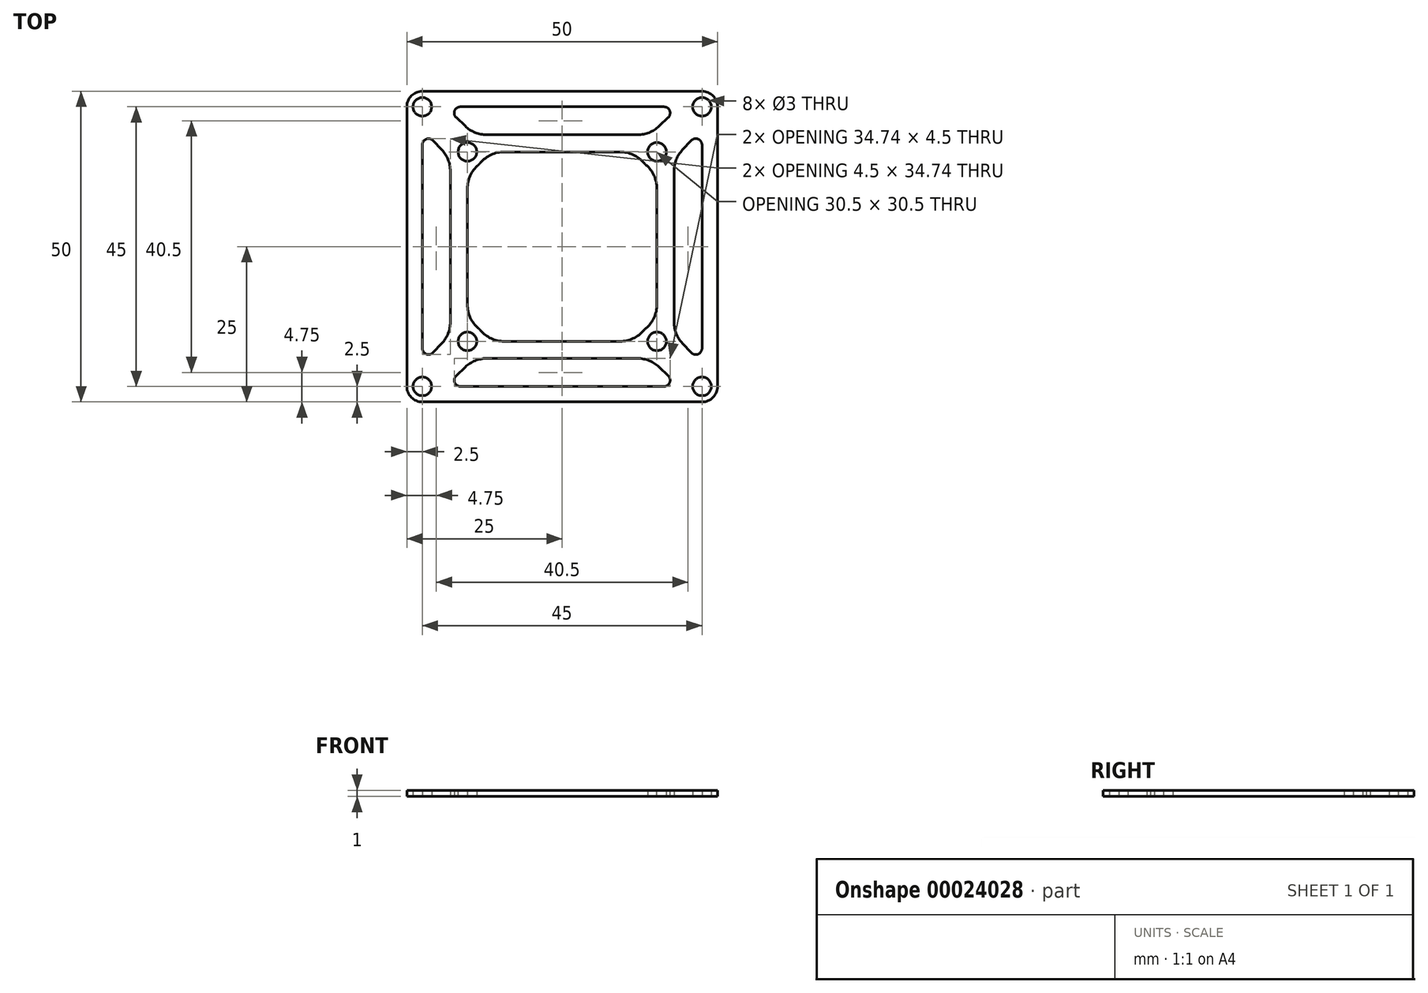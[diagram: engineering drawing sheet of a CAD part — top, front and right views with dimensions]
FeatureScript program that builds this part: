
annotation { "Feature Type Name" : "Feature", "Feature Type Description" : "" }
export const myFeature = defineFeature(function(context is Context, id is Id, definition is map)
    precondition{}
    {
        {
            var Q0;
            Q0=qCreatedBy(makeId("Top.planeOp"),FACE);
            var sketch = newSketch(context, id + "F0", { "sketchPlane" : qUnion([Q0])});
            skLineSegment(sketch, "E0.bottom", {"start": v(15.25, 15.25) * mm, "end": v(-15.25, 15.25) * mm});
            skLineSegment(sketch, "E0.top", {"start": v(15.25, -15.25) * mm, "end": v(-15.25, -15.25) * mm});
            skLineSegment(sketch, "E0.left", {"start": v(15.25, 15.25) * mm, "end": v(15.25, -15.25) * mm});
            skLineSegment(sketch, "E0.right", {"start": v(-15.25, 15.25) * mm, "end": v(-15.25, -15.25) * mm});
            skPoint(sketch, "E0.middle", {"position": v(0, 0) * mm});
            skLineSegment(sketch, "E1.bottom", {"start": v(22.5, 22.5) * mm, "end": v(-22.5, 22.5) * mm});
            skLineSegment(sketch, "E1.top", {"start": v(22.5, -22.5) * mm, "end": v(-22.5, -22.5) * mm});
            skLineSegment(sketch, "E1.left", {"start": v(22.5, 22.5) * mm, "end": v(22.5, -22.5) * mm});
            skLineSegment(sketch, "E1.right", {"start": v(-22.5, 22.5) * mm, "end": v(-22.5, -22.5) * mm});
            skLineSegment(sketch, "E2.bottom", {"start": v(-18, 18) * mm, "end": v(18, 18) * mm});
            skLineSegment(sketch, "E2.top", {"start": v(-18, -18) * mm, "end": v(18, -18) * mm});
            skLineSegment(sketch, "E2.left", {"start": v(-18, 18) * mm, "end": v(-18, -18) * mm});
            skLineSegment(sketch, "E2.right", {"start": v(18, 18) * mm, "end": v(18, -18) * mm});
            skLineSegment(sketch, "E3.bottom", {"start": v(-25, 25) * mm, "end": v(25, 25) * mm});
            skLineSegment(sketch, "E3.top", {"start": v(-25, -25) * mm, "end": v(25, -25) * mm});
            skLineSegment(sketch, "E3.left", {"start": v(-25, 25) * mm, "end": v(-25, -25) * mm});
            skLineSegment(sketch, "E3.right", {"start": v(25, 25) * mm, "end": v(25, -25) * mm});
            skCircle(sketch, "E4", {"center": v(-15.25, 15.25) * mm, "radius": 1.5 * mm});
            skCircle(sketch, "E5", {"center": v(-22.5, 22.5) * mm, "radius": 1.5 * mm});
            skLineSegment(sketch, "E6", {"start": v(0, 25) * mm, "end": v(0, 0) * mm, "construction": true});
            skLineSegment(sketch, "E7", {"start": v(0, 0) * mm, "end": v(-25, 0) * mm, "construction": true});
            skCircle(sketch, "E8.MirrorC", {"center": v(15.25, 15.25) * mm, "radius": 1.5 * mm});
            skCircle(sketch, "E9.MirrorC", {"center": v(22.5, 22.5) * mm, "radius": 1.5 * mm});
            skCircle(sketch, "E10.MirrorC", {"center": v(-15.25, -15.25) * mm, "radius": 1.5 * mm});
            skCircle(sketch, "E11.MirrorC", {"center": v(15.25, -15.25) * mm, "radius": 1.5 * mm});
            skCircle(sketch, "E12.MirrorC", {"center": v(22.5, -22.5) * mm, "radius": 1.5 * mm});
            skCircle(sketch, "E13.MirrorC", {"center": v(-22.5, -22.5) * mm, "radius": 1.5 * mm});
            skCircle(sketch, "E14", {"center": v(-22.5, 22.5) * mm, "radius": 2.5 * mm});
            skCircle(sketch, "E15", {"center": v(-15.25, 15.25) * mm, "radius": 2.75 * mm});
            skCircle(sketch, "E16.MirrorC", {"center": v(15.25, 15.25) * mm, "radius": 2.75 * mm});
            skCircle(sketch, "E17.MirrorC", {"center": v(22.5, 22.5) * mm, "radius": 2.5 * mm});
            skCircle(sketch, "E18.MirrorC", {"center": v(-15.25, -15.25) * mm, "radius": 2.75 * mm});
            skCircle(sketch, "E19.MirrorC", {"center": v(-22.5, -22.5) * mm, "radius": 2.5 * mm});
            skCircle(sketch, "E20.MirrorC", {"center": v(15.25, -15.25) * mm, "radius": 2.75 * mm});
            skCircle(sketch, "E21.MirrorC", {"center": v(22.5, -22.5) * mm, "radius": 2.5 * mm});
            skLineSegment(sketch, "E22", {"start": v(-13.35, 17.24) * mm, "end": v(-20.78, 24.31) * mm});
            skLineSegment(sketch, "E23", {"start": v(-17.24, 13.35) * mm, "end": v(-24.31, 20.78) * mm});
            skLineSegment(sketch, "E24.MirrorCS", {"start": v(13.35, 17.24) * mm, "end": v(20.78, 24.31) * mm});
            skLineSegment(sketch, "E25.MirrorCS", {"start": v(17.24, 13.35) * mm, "end": v(24.31, 20.78) * mm});
            skLineSegment(sketch, "E26.MirrorCS", {"start": v(-17.24, -13.35) * mm, "end": v(-24.31, -20.78) * mm});
            skLineSegment(sketch, "E27.MirrorCS", {"start": v(-13.35, -17.24) * mm, "end": v(-20.78, -24.31) * mm});
            skLineSegment(sketch, "E28.MirrorCS", {"start": v(17.24, -13.35) * mm, "end": v(24.31, -20.78) * mm});
            skLineSegment(sketch, "E29.MirrorCS", {"start": v(13.35, -17.24) * mm, "end": v(20.78, -24.31) * mm});
            skSolve(sketch);
        }
        {
            var Q0;
            {var subQ0=sQuery(id+"F0.wireOp",EDGE,"E17.MirrorC");var subQ1=sQuery(id+"F0.wireOp",EDGE,"E1.bottom");var subQ2=makeQuery(id+"F0.imprint","INTERSECT",VERTEX,{"derivedFrom":[subQ1,subQ0]});Q0=makeQuery(id+"F0.imprint","IMPRINT",FACE,{"disambiguationData":[TD([[makeQuery(id+"F0.imprint","IMPRINT",EDGE,{"disambiguationData":[TD([[subQ2,-1.0]])],"derivedFrom":subQ1}),-1.0]])]});}
            var Q1;
            {var subQ0=sQuery(id+"F0.wireOp",EDGE,"E21.MirrorC");var subQ1=sQuery(id+"F0.wireOp",EDGE,"E1.top");var subQ2=makeQuery(id+"F0.imprint","INTERSECT",VERTEX,{"derivedFrom":[subQ1,subQ0]});Q1=makeQuery(id+"F0.imprint","IMPRINT",FACE,{"disambiguationData":[TD([[makeQuery(id+"F0.imprint","IMPRINT",EDGE,{"disambiguationData":[TD([[subQ2,-1.0]])],"derivedFrom":subQ1}),1.0]])]});}
            var Q2;
            {var subQ0=sQuery(id+"F0.wireOp",EDGE,"E17.MirrorC");var subQ1=sQuery(id+"F0.wireOp",EDGE,"E1.left");var subQ2=makeQuery(id+"F0.imprint","INTERSECT",VERTEX,{"derivedFrom":[subQ1,subQ0]});Q2=makeQuery(id+"F0.imprint","IMPRINT",FACE,{"disambiguationData":[TD([[makeQuery(id+"F0.imprint","IMPRINT",EDGE,{"disambiguationData":[TD([[subQ2,-1.0]])],"derivedFrom":subQ1}),1.0]])]});}
            var Q3;
            {var subQ0=sQuery(id+"F0.wireOp",EDGE,"E14");var subQ1=sQuery(id+"F0.wireOp",EDGE,"E1.right");var subQ2=makeQuery(id+"F0.imprint","INTERSECT",VERTEX,{"derivedFrom":[subQ1,subQ0]});Q3=makeQuery(id+"F0.imprint","IMPRINT",FACE,{"disambiguationData":[TD([[makeQuery(id+"F0.imprint","IMPRINT",EDGE,{"disambiguationData":[TD([[subQ2,-1.0]])],"derivedFrom":subQ1}),-1.0]])]});}
            var Q4;
            {var subQ0=sQuery(id+"F0.wireOp",EDGE,"E9.MirrorC");var subQ1=sQuery(id+"F0.wireOp",EDGE,"E1.bottom");var subQ2=makeQuery(id+"F0.imprint","INTERSECT",VERTEX,{"derivedFrom":[subQ1,subQ0]});Q4=makeQuery(id+"F0.imprint","IMPRINT",FACE,{"disambiguationData":[TD([[makeQuery(id+"F0.imprint","IMPRINT",EDGE,{"disambiguationData":[TD([[subQ2,-1.0]])],"derivedFrom":subQ1}),-1.0]])]});}
            var Q5;
            {var subQ0=sQuery(id+"F0.wireOp",EDGE,"E14");var subQ2=sQuery(id+"F0.wireOp",EDGE,"E1.bottom");var subQ3=makeQuery(id+"F0.imprint","INTERSECT",VERTEX,{"derivedFrom":[subQ2,subQ0]});Q5=makeQuery(id+"F0.imprint","IMPRINT",FACE,{"disambiguationData":[TD([[makeQuery(id+"F0.imprint","IMPRINT",EDGE,{"disambiguationData":[TD([[subQ3,-1.0]])],"derivedFrom":subQ2}),-1.0]])]});}
            var Q6;
            {var subQ2=sQuery(id+"F0.wireOp",EDGE,"E1.top");var subQ4=sQuery(id+"F0.wireOp",EDGE,"E12.MirrorC");var subQ5=makeQuery(id+"F0.imprint","INTERSECT",VERTEX,{"derivedFrom":[subQ2,subQ4]});Q6=makeQuery(id+"F0.imprint","IMPRINT",FACE,{"disambiguationData":[TD([[makeQuery(id+"F0.imprint","IMPRINT",EDGE,{"disambiguationData":[TD([[subQ5,-1.0]])],"derivedFrom":subQ2}),1.0]])]});}
            var Q7;
            {var subQ1=sQuery(id+"F0.wireOp",EDGE,"E1.top");var subQ5=sQuery(id+"F0.wireOp",EDGE,"E19.MirrorC");var subQ7=makeQuery(id+"F0.imprint","INTERSECT",VERTEX,{"derivedFrom":[subQ1,subQ5]});Q7=makeQuery(id+"F0.imprint","IMPRINT",FACE,{"disambiguationData":[TD([[makeQuery(id+"F0.imprint","IMPRINT",EDGE,{"disambiguationData":[TD([[subQ7,-1.0]])],"derivedFrom":subQ1}),1.0]])]});}
            var Q8;
            {var subQ0=sQuery(id+"F0.wireOp",EDGE,"E14");var subQ1=sQuery(id+"F0.wireOp",EDGE,"E1.bottom");var subQ2=makeQuery(id+"F0.imprint","INTERSECT",VERTEX,{"derivedFrom":[subQ1,subQ0]});Q8=makeQuery(id+"F0.imprint","IMPRINT",FACE,{"disambiguationData":[TD([[makeQuery(id+"F0.imprint","IMPRINT",EDGE,{"disambiguationData":[TD([[subQ2,-1.0]])],"derivedFrom":subQ1}),1.0]])]});}
            var Q9;
            {var subQ0=sQuery(id+"F0.wireOp",EDGE,"E9.MirrorC");var subQ1=sQuery(id+"F0.wireOp",EDGE,"E1.bottom");var subQ2=makeQuery(id+"F0.imprint","INTERSECT",VERTEX,{"derivedFrom":[subQ1,subQ0]});Q9=makeQuery(id+"F0.imprint","IMPRINT",FACE,{"disambiguationData":[TD([[makeQuery(id+"F0.imprint","IMPRINT",EDGE,{"disambiguationData":[TD([[subQ2,-1.0]])],"derivedFrom":subQ1}),1.0]])]});}
            var Q10;
            {var subQ0=sQuery(id+"F0.wireOp",EDGE,"E12.MirrorC");var subQ1=sQuery(id+"F0.wireOp",EDGE,"E1.top");var subQ2=makeQuery(id+"F0.imprint","INTERSECT",VERTEX,{"derivedFrom":[subQ1,subQ0]});Q10=makeQuery(id+"F0.imprint","IMPRINT",FACE,{"disambiguationData":[TD([[makeQuery(id+"F0.imprint","IMPRINT",EDGE,{"disambiguationData":[TD([[subQ2,-1.0]])],"derivedFrom":subQ1}),-1.0]])]});}
            var Q11;
            {var subQ0=sQuery(id+"F0.wireOp",EDGE,"E19.MirrorC");var subQ1=sQuery(id+"F0.wireOp",EDGE,"E1.top");var subQ2=makeQuery(id+"F0.imprint","INTERSECT",VERTEX,{"derivedFrom":[subQ1,subQ0]});Q11=makeQuery(id+"F0.imprint","IMPRINT",FACE,{"disambiguationData":[TD([[makeQuery(id+"F0.imprint","IMPRINT",EDGE,{"disambiguationData":[TD([[subQ2,-1.0]])],"derivedFrom":subQ1}),-1.0]])]});}
            var Q12;
            {var subQ16=sQuery(id+"F0.wireOp",EDGE,"E1.bottom");var subQ30=sQuery(id+"F0.wireOp",EDGE,"E17.MirrorC");var subQ31=makeQuery(id+"F0.imprint","INTERSECT",VERTEX,{"derivedFrom":[subQ16,subQ30]});Q12=makeQuery(id+"F0.imprint","IMPRINT",FACE,{"disambiguationData":[TD([[makeQuery(id+"F0.imprint","IMPRINT",EDGE,{"disambiguationData":[TD([[subQ31,-1.0]])],"derivedFrom":subQ16}),1.0]])]});}
            var Q13;
            {var subQ0=sQuery(id+"F0.wireOp",EDGE,"E18.MirrorC");var subQ1=sQuery(id+"F0.wireOp",EDGE,"E0.top");var subQ2=makeQuery(id+"F0.imprint","INTERSECT",VERTEX,{"derivedFrom":[subQ1,subQ0]});Q13=makeQuery(id+"F0.imprint","IMPRINT",FACE,{"disambiguationData":[TD([[makeQuery(id+"F0.imprint","IMPRINT",EDGE,{"disambiguationData":[TD([[subQ2,-1.0]])],"derivedFrom":subQ1}),-1.0]])]});}
            var Q14;
            {var subQ0=sQuery(id+"F0.wireOp",EDGE,"E18.MirrorC");var subQ1=sQuery(id+"F0.wireOp",EDGE,"E0.top");var subQ2=makeQuery(id+"F0.imprint","INTERSECT",VERTEX,{"derivedFrom":[subQ1,subQ0]});Q14=makeQuery(id+"F0.imprint","IMPRINT",FACE,{"disambiguationData":[TD([[makeQuery(id+"F0.imprint","IMPRINT",EDGE,{"disambiguationData":[TD([[subQ2,-1.0]])],"derivedFrom":subQ1}),1.0]])]});}
            var Q15;
            {var subQ0=sQuery(id+"F0.wireOp",EDGE,"E2.left");var subQ1=sQuery(id+"F0.wireOp",EDGE,"E2.top");var subQ2=makeQuery(id+"F0.imprint","INTERSECT",VERTEX,{"derivedFrom":[subQ1,subQ0]});Q15=makeQuery(id+"F0.imprint","IMPRINT",FACE,{"disambiguationData":[TD([[makeQuery(id+"F0.imprint","IMPRINT",EDGE,{"disambiguationData":[TD([[subQ2,-1.0]])],"derivedFrom":subQ1}),1.0]])]});}
            var Q16;
            {var subQ0=sQuery(id+"F0.wireOp",EDGE,"E20.MirrorC");var subQ1=sQuery(id+"F0.wireOp",EDGE,"E0.top");var subQ2=makeQuery(id+"F0.imprint","INTERSECT",VERTEX,{"derivedFrom":[subQ1,subQ0]});Q16=makeQuery(id+"F0.imprint","IMPRINT",FACE,{"disambiguationData":[TD([[makeQuery(id+"F0.imprint","IMPRINT",EDGE,{"disambiguationData":[TD([[subQ2,-1.0]])],"derivedFrom":subQ1}),1.0]])]});}
            var Q17;
            {var subQ0=sQuery(id+"F0.wireOp",EDGE,"E15");var subQ1=sQuery(id+"F0.wireOp",EDGE,"E0.right");var subQ2=makeQuery(id+"F0.imprint","INTERSECT",VERTEX,{"derivedFrom":[subQ1,subQ0]});Q17=makeQuery(id+"F0.imprint","IMPRINT",FACE,{"disambiguationData":[TD([[makeQuery(id+"F0.imprint","IMPRINT",EDGE,{"disambiguationData":[TD([[subQ2,-1.0]])],"derivedFrom":subQ1}),-1.0]])]});}
            var Q18;
            {var subQ0=sQuery(id+"F0.wireOp",EDGE,"E16.MirrorC");var subQ1=sQuery(id+"F0.wireOp",EDGE,"E0.bottom");var subQ2=makeQuery(id+"F0.imprint","INTERSECT",VERTEX,{"derivedFrom":[subQ1,subQ0]});Q18=makeQuery(id+"F0.imprint","IMPRINT",FACE,{"disambiguationData":[TD([[makeQuery(id+"F0.imprint","IMPRINT",EDGE,{"disambiguationData":[TD([[subQ2,-1.0]])],"derivedFrom":subQ1}),-1.0]])]});}
            var Q19;
            {var subQ0=sQuery(id+"F0.wireOp",EDGE,"E16.MirrorC");var subQ1=sQuery(id+"F0.wireOp",EDGE,"E0.left");var subQ2=makeQuery(id+"F0.imprint","INTERSECT",VERTEX,{"derivedFrom":[subQ1,subQ0]});Q19=makeQuery(id+"F0.imprint","IMPRINT",FACE,{"disambiguationData":[TD([[makeQuery(id+"F0.imprint","IMPRINT",EDGE,{"disambiguationData":[TD([[subQ2,-1.0]])],"derivedFrom":subQ1}),1.0]])]});}
            var Q20;
            {var subQ1=sQuery(id+"F0.wireOp",EDGE,"E0.top");var subQ4=sQuery(id+"F0.wireOp",EDGE,"E11.MirrorC");var subQ5=makeQuery(id+"F0.imprint","INTERSECT",VERTEX,{"derivedFrom":[subQ1,subQ4]});Q20=makeQuery(id+"F0.imprint","IMPRINT",FACE,{"disambiguationData":[TD([[makeQuery(id+"F0.imprint","IMPRINT",EDGE,{"disambiguationData":[TD([[subQ5,-1.0]])],"derivedFrom":subQ1}),1.0]])]});}
            var Q21;
            {var subQ0=sQuery(id+"F0.wireOp",EDGE,"E11.MirrorC");var subQ1=sQuery(id+"F0.wireOp",EDGE,"E0.top");var subQ2=makeQuery(id+"F0.imprint","INTERSECT",VERTEX,{"derivedFrom":[subQ1,subQ0]});Q21=makeQuery(id+"F0.imprint","IMPRINT",FACE,{"disambiguationData":[TD([[makeQuery(id+"F0.imprint","IMPRINT",EDGE,{"disambiguationData":[TD([[subQ2,-1.0]])],"derivedFrom":subQ1}),-1.0]])]});}
            var Q22;
            {var subQ0=sQuery(id+"F0.wireOp",EDGE,"E2.right");var subQ1=sQuery(id+"F0.wireOp",EDGE,"E2.top");var subQ2=makeQuery(id+"F0.imprint","INTERSECT",VERTEX,{"derivedFrom":[subQ1,subQ0]});Q22=makeQuery(id+"F0.imprint","IMPRINT",FACE,{"disambiguationData":[TD([[makeQuery(id+"F0.imprint","IMPRINT",EDGE,{"disambiguationData":[TD([[subQ2,1.0]])],"derivedFrom":subQ1}),1.0]])]});}
            var Q23;
            {var subQ0=sQuery(id+"F0.wireOp",EDGE,"E15");var subQ1=sQuery(id+"F0.wireOp",EDGE,"E0.bottom");var subQ2=makeQuery(id+"F0.imprint","INTERSECT",VERTEX,{"derivedFrom":[subQ1,subQ0]});Q23=makeQuery(id+"F0.imprint","IMPRINT",FACE,{"disambiguationData":[TD([[makeQuery(id+"F0.imprint","IMPRINT",EDGE,{"disambiguationData":[TD([[subQ2,-1.0]])],"derivedFrom":subQ1}),1.0]])]});}
            var Q24;
            {var subQ0=sQuery(id+"F0.wireOp",EDGE,"E2.left");var subQ1=sQuery(id+"F0.wireOp",EDGE,"E2.bottom");var subQ2=makeQuery(id+"F0.imprint","INTERSECT",VERTEX,{"derivedFrom":[subQ1,subQ0]});Q24=makeQuery(id+"F0.imprint","IMPRINT",FACE,{"disambiguationData":[TD([[makeQuery(id+"F0.imprint","IMPRINT",EDGE,{"disambiguationData":[TD([[subQ2,-1.0]])],"derivedFrom":subQ1}),-1.0]])]});}
            var Q25;
            {var subQ1=sQuery(id+"F0.wireOp",EDGE,"E0.bottom");var subQ5=sQuery(id+"F0.wireOp",EDGE,"E15");var subQ6=makeQuery(id+"F0.imprint","INTERSECT",VERTEX,{"derivedFrom":[subQ1,subQ5]});Q25=makeQuery(id+"F0.imprint","IMPRINT",FACE,{"disambiguationData":[TD([[makeQuery(id+"F0.imprint","IMPRINT",EDGE,{"disambiguationData":[TD([[subQ6,-1.0]])],"derivedFrom":subQ1}),-1.0]])]});}
            var Q26;
            {var subQ0=sQuery(id+"F0.wireOp",EDGE,"E2.right");var subQ1=sQuery(id+"F0.wireOp",EDGE,"E2.bottom");var subQ2=makeQuery(id+"F0.imprint","INTERSECT",VERTEX,{"derivedFrom":[subQ1,subQ0]});Q26=makeQuery(id+"F0.imprint","IMPRINT",FACE,{"disambiguationData":[TD([[makeQuery(id+"F0.imprint","IMPRINT",EDGE,{"disambiguationData":[TD([[subQ2,1.0]])],"derivedFrom":subQ1}),-1.0]])]});}
            var Q27;
            {var subQ1=sQuery(id+"F0.wireOp",EDGE,"E0.bottom");var subQ4=sQuery(id+"F0.wireOp",EDGE,"E8.MirrorC");var subQ8=makeQuery(id+"F0.imprint","INTERSECT",VERTEX,{"derivedFrom":[subQ1,subQ4]});Q27=makeQuery(id+"F0.imprint","IMPRINT",FACE,{"disambiguationData":[TD([[makeQuery(id+"F0.imprint","IMPRINT",EDGE,{"disambiguationData":[TD([[subQ8,-1.0]])],"derivedFrom":subQ1}),-1.0]])]});}
            var Q28;
            {var subQ0=sQuery(id+"F0.wireOp",EDGE,"E8.MirrorC");var subQ1=sQuery(id+"F0.wireOp",EDGE,"E0.bottom");var subQ2=makeQuery(id+"F0.imprint","INTERSECT",VERTEX,{"derivedFrom":[subQ1,subQ0]});Q28=makeQuery(id+"F0.imprint","IMPRINT",FACE,{"disambiguationData":[TD([[makeQuery(id+"F0.imprint","IMPRINT",EDGE,{"disambiguationData":[TD([[subQ2,-1.0]])],"derivedFrom":subQ1}),1.0]])]});}
            var Q29;
            {var subQ5=sQuery(id+"F0.wireOp",EDGE,"E24.MirrorCS");var subQ9=sQuery(id+"F0.wireOp",EDGE,"E1.bottom");var subQ11=makeQuery(id+"F0.imprint","INTERSECT",VERTEX,{"derivedFrom":[subQ9,subQ5]});Q29=makeQuery(id+"F0.imprint","IMPRINT",FACE,{"disambiguationData":[TD([[makeQuery(id+"F0.imprint","IMPRINT",EDGE,{"disambiguationData":[TD([[subQ11,-1.0]])],"derivedFrom":subQ9}),-1.0]])]});}
            var Q30;
            {var subQ0=sQuery(id+"F0.wireOp",EDGE,"E22");var subQ1=sQuery(id+"F0.wireOp",EDGE,"E1.bottom");var subQ2=makeQuery(id+"F0.imprint","INTERSECT",VERTEX,{"derivedFrom":[subQ1,subQ0]});Q30=makeQuery(id+"F0.imprint","IMPRINT",FACE,{"disambiguationData":[TD([[makeQuery(id+"F0.imprint","IMPRINT",EDGE,{"disambiguationData":[TD([[subQ2,-1.0]])],"derivedFrom":subQ1}),-1.0]])]});}
            var Q31;
            {var subQ3=sQuery(id+"F0.wireOp",EDGE,"E22");var subQ7=sQuery(id+"F0.wireOp",EDGE,"E1.bottom");var subQ8=makeQuery(id+"F0.imprint","INTERSECT",VERTEX,{"derivedFrom":[subQ7,subQ3]});Q31=makeQuery(id+"F0.imprint","IMPRINT",FACE,{"disambiguationData":[TD([[makeQuery(id+"F0.imprint","IMPRINT",EDGE,{"disambiguationData":[TD([[subQ8,-1.0]])],"derivedFrom":subQ7}),1.0]])]});}
            var Q32;
            {var subQ5=sQuery(id+"F0.wireOp",EDGE,"E23");var subQ8=sQuery(id+"F0.wireOp",EDGE,"E1.right");var subQ9=makeQuery(id+"F0.imprint","INTERSECT",VERTEX,{"derivedFrom":[subQ8,subQ5]});Q32=makeQuery(id+"F0.imprint","IMPRINT",FACE,{"disambiguationData":[TD([[makeQuery(id+"F0.imprint","IMPRINT",EDGE,{"disambiguationData":[TD([[subQ9,-1.0]])],"derivedFrom":subQ8}),-1.0]])]});}
            var Q33;
            {var subQ5=sQuery(id+"F0.wireOp",EDGE,"E25.MirrorCS");var subQ9=sQuery(id+"F0.wireOp",EDGE,"E1.left");var subQ10=makeQuery(id+"F0.imprint","INTERSECT",VERTEX,{"derivedFrom":[subQ9,subQ5]});Q33=makeQuery(id+"F0.imprint","IMPRINT",FACE,{"disambiguationData":[TD([[makeQuery(id+"F0.imprint","IMPRINT",EDGE,{"disambiguationData":[TD([[subQ10,-1.0]])],"derivedFrom":subQ9}),1.0]])]});}
            var Q34;
            {var subQ8=sQuery(id+"F0.wireOp",EDGE,"E21.MirrorC");var subQ12=sQuery(id+"F0.wireOp",EDGE,"E1.top");var subQ13=makeQuery(id+"F0.imprint","INTERSECT",VERTEX,{"derivedFrom":[subQ12,subQ8]});Q34=makeQuery(id+"F0.imprint","IMPRINT",FACE,{"disambiguationData":[TD([[makeQuery(id+"F0.imprint","IMPRINT",EDGE,{"disambiguationData":[TD([[subQ13,-1.0]])],"derivedFrom":subQ12}),-1.0]])]});}
            var Q35;
            {var subQ0=sQuery(id+"F0.wireOp",EDGE,"E29.MirrorCS");var subQ9=sQuery(id+"F0.wireOp",EDGE,"E1.top");var subQ10=makeQuery(id+"F0.imprint","INTERSECT",VERTEX,{"derivedFrom":[subQ9,subQ0]});Q35=makeQuery(id+"F0.imprint","IMPRINT",FACE,{"disambiguationData":[TD([[makeQuery(id+"F0.imprint","IMPRINT",EDGE,{"disambiguationData":[TD([[subQ10,-1.0]])],"derivedFrom":subQ9}),1.0]])]});}
            var Q36;
            {var subQ0=sQuery(id+"F0.wireOp",EDGE,"E28.MirrorCS");var subQ1=sQuery(id+"F0.wireOp",EDGE,"E1.left");var subQ2=makeQuery(id+"F0.imprint","INTERSECT",VERTEX,{"derivedFrom":[subQ1,subQ0]});Q36=makeQuery(id+"F0.imprint","IMPRINT",FACE,{"disambiguationData":[TD([[makeQuery(id+"F0.imprint","IMPRINT",EDGE,{"disambiguationData":[TD([[subQ2,-1.0]])],"derivedFrom":subQ1}),1.0]])]});}
            var Q37;
            {var subQ3=sQuery(id+"F0.wireOp",EDGE,"E27.MirrorCS");var subQ12=sQuery(id+"F0.wireOp",EDGE,"E1.top");var subQ13=makeQuery(id+"F0.imprint","INTERSECT",VERTEX,{"derivedFrom":[subQ12,subQ3]});Q37=makeQuery(id+"F0.imprint","IMPRINT",FACE,{"disambiguationData":[TD([[makeQuery(id+"F0.imprint","IMPRINT",EDGE,{"disambiguationData":[TD([[subQ13,-1.0]])],"derivedFrom":subQ12}),-1.0]])]});}
            var Q38;
            {var subQ0=sQuery(id+"F0.wireOp",EDGE,"E27.MirrorCS");var subQ1=sQuery(id+"F0.wireOp",EDGE,"E1.top");var subQ2=makeQuery(id+"F0.imprint","INTERSECT",VERTEX,{"derivedFrom":[subQ1,subQ0]});Q38=makeQuery(id+"F0.imprint","IMPRINT",FACE,{"disambiguationData":[TD([[makeQuery(id+"F0.imprint","IMPRINT",EDGE,{"disambiguationData":[TD([[subQ2,-1.0]])],"derivedFrom":subQ1}),1.0]])]});}
            var Q39;
            {var subQ0=sQuery(id+"F0.wireOp",EDGE,"E26.MirrorCS");var subQ1=sQuery(id+"F0.wireOp",EDGE,"E1.right");var subQ2=makeQuery(id+"F0.imprint","INTERSECT",VERTEX,{"derivedFrom":[subQ1,subQ0]});Q39=makeQuery(id+"F0.imprint","IMPRINT",FACE,{"disambiguationData":[TD([[makeQuery(id+"F0.imprint","IMPRINT",EDGE,{"disambiguationData":[TD([[subQ2,-1.0]])],"derivedFrom":subQ1}),-1.0]])]});}
            var Q40;
            {var subQ0=sQuery(id+"F0.wireOp",EDGE,"E26.MirrorCS");var subQ1=sQuery(id+"F0.wireOp",EDGE,"E2.left");var subQ2=makeQuery(id+"F0.imprint","INTERSECT",VERTEX,{"derivedFrom":[subQ1,subQ0]});Q40=makeQuery(id+"F0.imprint","IMPRINT",FACE,{"disambiguationData":[TD([[makeQuery(id+"F0.imprint","IMPRINT",EDGE,{"disambiguationData":[TD([[subQ2,-1.0]])],"derivedFrom":subQ1}),1.0]])]});}
            var Q41;
            {var subQ0=sQuery(id+"F0.wireOp",EDGE,"E18.MirrorC");var subQ1=sQuery(id+"F0.wireOp",EDGE,"E2.top");var subQ2=makeQuery(id+"F0.imprint","INTERSECT",VERTEX,{"derivedFrom":[subQ1,subQ0]});Q41=makeQuery(id+"F0.imprint","IMPRINT",FACE,{"disambiguationData":[TD([[makeQuery(id+"F0.imprint","IMPRINT",EDGE,{"disambiguationData":[TD([[subQ2,-1.0]])],"derivedFrom":subQ1}),1.0]])]});}
            var Q42;
            {var subQ0=sQuery(id+"F0.wireOp",EDGE,"E15");var subQ1=sQuery(id+"F0.wireOp",EDGE,"E2.left");var subQ2=makeQuery(id+"F0.imprint","INTERSECT",VERTEX,{"derivedFrom":[subQ1,subQ0]});Q42=makeQuery(id+"F0.imprint","IMPRINT",FACE,{"disambiguationData":[TD([[makeQuery(id+"F0.imprint","IMPRINT",EDGE,{"disambiguationData":[TD([[subQ2,-1.0]])],"derivedFrom":subQ1}),1.0]])]});}
            var Q43;
            {var subQ0=sQuery(id+"F0.wireOp",EDGE,"E15");var subQ1=sQuery(id+"F0.wireOp",EDGE,"E2.bottom");var subQ2=makeQuery(id+"F0.imprint","INTERSECT",VERTEX,{"derivedFrom":[subQ1,subQ0]});Q43=makeQuery(id+"F0.imprint","IMPRINT",FACE,{"disambiguationData":[TD([[makeQuery(id+"F0.imprint","IMPRINT",EDGE,{"disambiguationData":[TD([[subQ2,-1.0]])],"derivedFrom":subQ1}),-1.0]])]});}
            var Q44;
            {var subQ0=sQuery(id+"F0.wireOp",EDGE,"E24.MirrorCS");var subQ1=sQuery(id+"F0.wireOp",EDGE,"E2.bottom");var subQ2=makeQuery(id+"F0.imprint","INTERSECT",VERTEX,{"derivedFrom":[subQ1,subQ0]});Q44=makeQuery(id+"F0.imprint","IMPRINT",FACE,{"disambiguationData":[TD([[makeQuery(id+"F0.imprint","IMPRINT",EDGE,{"disambiguationData":[TD([[subQ2,-1.0]])],"derivedFrom":subQ1}),-1.0]])]});}
            var Q45;
            {var subQ0=sQuery(id+"F0.wireOp",EDGE,"E16.MirrorC");var subQ1=sQuery(id+"F0.wireOp",EDGE,"E2.right");var subQ2=makeQuery(id+"F0.imprint","INTERSECT",VERTEX,{"derivedFrom":[subQ1,subQ0]});Q45=makeQuery(id+"F0.imprint","IMPRINT",FACE,{"disambiguationData":[TD([[makeQuery(id+"F0.imprint","IMPRINT",EDGE,{"disambiguationData":[TD([[subQ2,-1.0]])],"derivedFrom":subQ1}),-1.0]])]});}
            var Q46;
            {var subQ0=sQuery(id+"F0.wireOp",EDGE,"E29.MirrorCS");var subQ1=sQuery(id+"F0.wireOp",EDGE,"E2.top");var subQ2=makeQuery(id+"F0.imprint","INTERSECT",VERTEX,{"derivedFrom":[subQ1,subQ0]});Q46=makeQuery(id+"F0.imprint","IMPRINT",FACE,{"disambiguationData":[TD([[makeQuery(id+"F0.imprint","IMPRINT",EDGE,{"disambiguationData":[TD([[subQ2,-1.0]])],"derivedFrom":subQ1}),1.0]])]});}
            var Q47;
            {var subQ0=sQuery(id+"F0.wireOp",EDGE,"E28.MirrorCS");var subQ1=sQuery(id+"F0.wireOp",EDGE,"E2.right");var subQ2=makeQuery(id+"F0.imprint","INTERSECT",VERTEX,{"derivedFrom":[subQ1,subQ0]});Q47=makeQuery(id+"F0.imprint","IMPRINT",FACE,{"disambiguationData":[TD([[makeQuery(id+"F0.imprint","IMPRINT",EDGE,{"disambiguationData":[TD([[subQ2,-1.0]])],"derivedFrom":subQ1}),-1.0]])]});}
            extrude(context, id + "F1", {"entities" : qUnion([Q0, Q1, Q2, Q3, Q4, Q5, Q6, Q7, Q8, Q9, Q10, Q11, Q12, Q13, Q14, Q15, Q16, Q17, Q18, Q19, Q20, Q21, Q22, Q23, Q24, Q25, Q26, Q27, Q28, Q29, Q30, Q31, Q32, Q33, Q34, Q35, Q36, Q37, Q38, Q39, Q40, Q41, Q42, Q43, Q44, Q45, Q46, Q47]), "depth" : 1 * mm});
        }
        {
            var Q0;
            Q0=makeQuery(id+"F1.opExtrude","SWEPT_EDGE",EDGE,{"disambiguationData":[OSD([sQuery(id+"F0.wireOp",EDGE,"E0.bottom"),sQuery(id+"F0.wireOp",EDGE,"E15")])]});
            var Q1;
            Q1=makeQuery(id+"F1.opExtrude","SWEPT_EDGE",EDGE,{"disambiguationData":[OSD([sQuery(id+"F0.wireOp",EDGE,"E0.right"),sQuery(id+"F0.wireOp",EDGE,"E15")])]});
            var Q2;
            Q2=makeQuery(id+"F1.opExtrude","SWEPT_EDGE",EDGE,{"disambiguationData":[OSD([sQuery(id+"F0.wireOp",EDGE,"E0.bottom"),sQuery(id+"F0.wireOp",EDGE,"E16.MirrorC")])]});
            var Q3;
            Q3=makeQuery(id+"F1.opExtrude","SWEPT_EDGE",EDGE,{"disambiguationData":[OSD([sQuery(id+"F0.wireOp",EDGE,"E0.left"),sQuery(id+"F0.wireOp",EDGE,"E16.MirrorC")])]});
            var Q4;
            Q4=makeQuery(id+"F1.opExtrude","SWEPT_EDGE",EDGE,{"disambiguationData":[OSD([sQuery(id+"F0.wireOp",EDGE,"E0.left"),sQuery(id+"F0.wireOp",EDGE,"E20.MirrorC")])]});
            var Q5;
            Q5=makeQuery(id+"F1.opExtrude","SWEPT_EDGE",EDGE,{"disambiguationData":[OSD([sQuery(id+"F0.wireOp",EDGE,"E0.top"),sQuery(id+"F0.wireOp",EDGE,"E20.MirrorC")])]});
            var Q6;
            Q6=makeQuery(id+"F1.opExtrude","SWEPT_EDGE",EDGE,{"disambiguationData":[OSD([sQuery(id+"F0.wireOp",EDGE,"E0.top"),sQuery(id+"F0.wireOp",EDGE,"E18.MirrorC")])]});
            var Q7;
            Q7=makeQuery(id+"F1.opExtrude","SWEPT_EDGE",EDGE,{"disambiguationData":[OSD([sQuery(id+"F0.wireOp",EDGE,"E0.right"),sQuery(id+"F0.wireOp",EDGE,"E18.MirrorC")])]});
            var Q8;
            Q8=makeQuery(id+"F1.opExtrude","SWEPT_EDGE",EDGE,{"disambiguationData":[OSD([sQuery(id+"F0.wireOp",EDGE,"E2.right"),sQuery(id+"F0.wireOp",EDGE,"E25.MirrorCS")])]});
            var Q9;
            Q9=makeQuery(id+"F1.opExtrude","SWEPT_EDGE",EDGE,{"disambiguationData":[OSD([sQuery(id+"F0.wireOp",EDGE,"E2.right"),sQuery(id+"F0.wireOp",EDGE,"E28.MirrorCS")])]});
            var Q10;
            Q10=makeQuery(id+"F1.opExtrude","SWEPT_EDGE",EDGE,{"disambiguationData":[OSD([sQuery(id+"F0.wireOp",EDGE,"E2.top"),sQuery(id+"F0.wireOp",EDGE,"E29.MirrorCS")])]});
            var Q11;
            Q11=makeQuery(id+"F1.opExtrude","SWEPT_EDGE",EDGE,{"disambiguationData":[OSD([sQuery(id+"F0.wireOp",EDGE,"E2.top"),sQuery(id+"F0.wireOp",EDGE,"E27.MirrorCS")])]});
            var Q12;
            Q12=makeQuery(id+"F1.opExtrude","SWEPT_EDGE",EDGE,{"disambiguationData":[OSD([sQuery(id+"F0.wireOp",EDGE,"E2.left"),sQuery(id+"F0.wireOp",EDGE,"E26.MirrorCS")])]});
            var Q13;
            Q13=makeQuery(id+"F1.opExtrude","SWEPT_EDGE",EDGE,{"disambiguationData":[OSD([sQuery(id+"F0.wireOp",EDGE,"E2.bottom"),sQuery(id+"F0.wireOp",EDGE,"E22")])]});
            var Q14;
            Q14=makeQuery(id+"F1.opExtrude","SWEPT_EDGE",EDGE,{"disambiguationData":[OSD([sQuery(id+"F0.wireOp",EDGE,"E2.left"),sQuery(id+"F0.wireOp",EDGE,"E23")])]});
            var Q15;
            Q15=makeQuery(id+"F1.opExtrude","SWEPT_EDGE",EDGE,{"disambiguationData":[OSD([sQuery(id+"F0.wireOp",EDGE,"E2.bottom"),sQuery(id+"F0.wireOp",EDGE,"E24.MirrorCS")])]});
            fillet(context, id + "F2", {"entities" : qUnion([Q0, Q1, Q2, Q3, Q4, Q5, Q6, Q7, Q8, Q9, Q10, Q11, Q12, Q13, Q14, Q15]), "radius" : 5 * mm, "tangentPropagation" : true, "allowEdgeOverflow" : false});
        }
        {
            var Q0;
            Q0=makeQuery(id+"F1.opExtrude","SWEPT_EDGE",EDGE,{"disambiguationData":[OSD([sQuery(id+"F0.wireOp",EDGE,"E1.right"),sQuery(id+"F0.wireOp",EDGE,"E26.MirrorCS")])]});
            var Q1;
            Q1=makeQuery(id+"F1.opExtrude","SWEPT_EDGE",EDGE,{"disambiguationData":[OSD([sQuery(id+"F0.wireOp",EDGE,"E1.right"),sQuery(id+"F0.wireOp",EDGE,"E23")])]});
            var Q2;
            Q2=makeQuery(id+"F1.opExtrude","SWEPT_EDGE",EDGE,{"disambiguationData":[OSD([sQuery(id+"F0.wireOp",EDGE,"E1.bottom"),sQuery(id+"F0.wireOp",EDGE,"E22")])]});
            var Q3;
            Q3=makeQuery(id+"F1.opExtrude","SWEPT_EDGE",EDGE,{"disambiguationData":[OSD([sQuery(id+"F0.wireOp",EDGE,"E1.bottom"),sQuery(id+"F0.wireOp",EDGE,"E24.MirrorCS")])]});
            var Q4;
            Q4=makeQuery(id+"F1.opExtrude","SWEPT_EDGE",EDGE,{"disambiguationData":[OSD([sQuery(id+"F0.wireOp",EDGE,"E1.left"),sQuery(id+"F0.wireOp",EDGE,"E25.MirrorCS")])]});
            var Q5;
            Q5=makeQuery(id+"F1.opExtrude","SWEPT_EDGE",EDGE,{"disambiguationData":[OSD([sQuery(id+"F0.wireOp",EDGE,"E1.left"),sQuery(id+"F0.wireOp",EDGE,"E28.MirrorCS")])]});
            var Q6;
            Q6=makeQuery(id+"F1.opExtrude","SWEPT_EDGE",EDGE,{"disambiguationData":[OSD([sQuery(id+"F0.wireOp",EDGE,"E1.top"),sQuery(id+"F0.wireOp",EDGE,"E27.MirrorCS")])]});
            var Q7;
            Q7=makeQuery(id+"F1.opExtrude","SWEPT_EDGE",EDGE,{"disambiguationData":[OSD([sQuery(id+"F0.wireOp",EDGE,"E1.top"),sQuery(id+"F0.wireOp",EDGE,"E29.MirrorCS")])]});
            fillet(context, id + "F3", {"entities" : qUnion([Q0, Q1, Q2, Q3, Q4, Q5, Q6, Q7]), "radius" : 1 * mm, "tangentPropagation" : true, "allowEdgeOverflow" : false});
        }
    });
